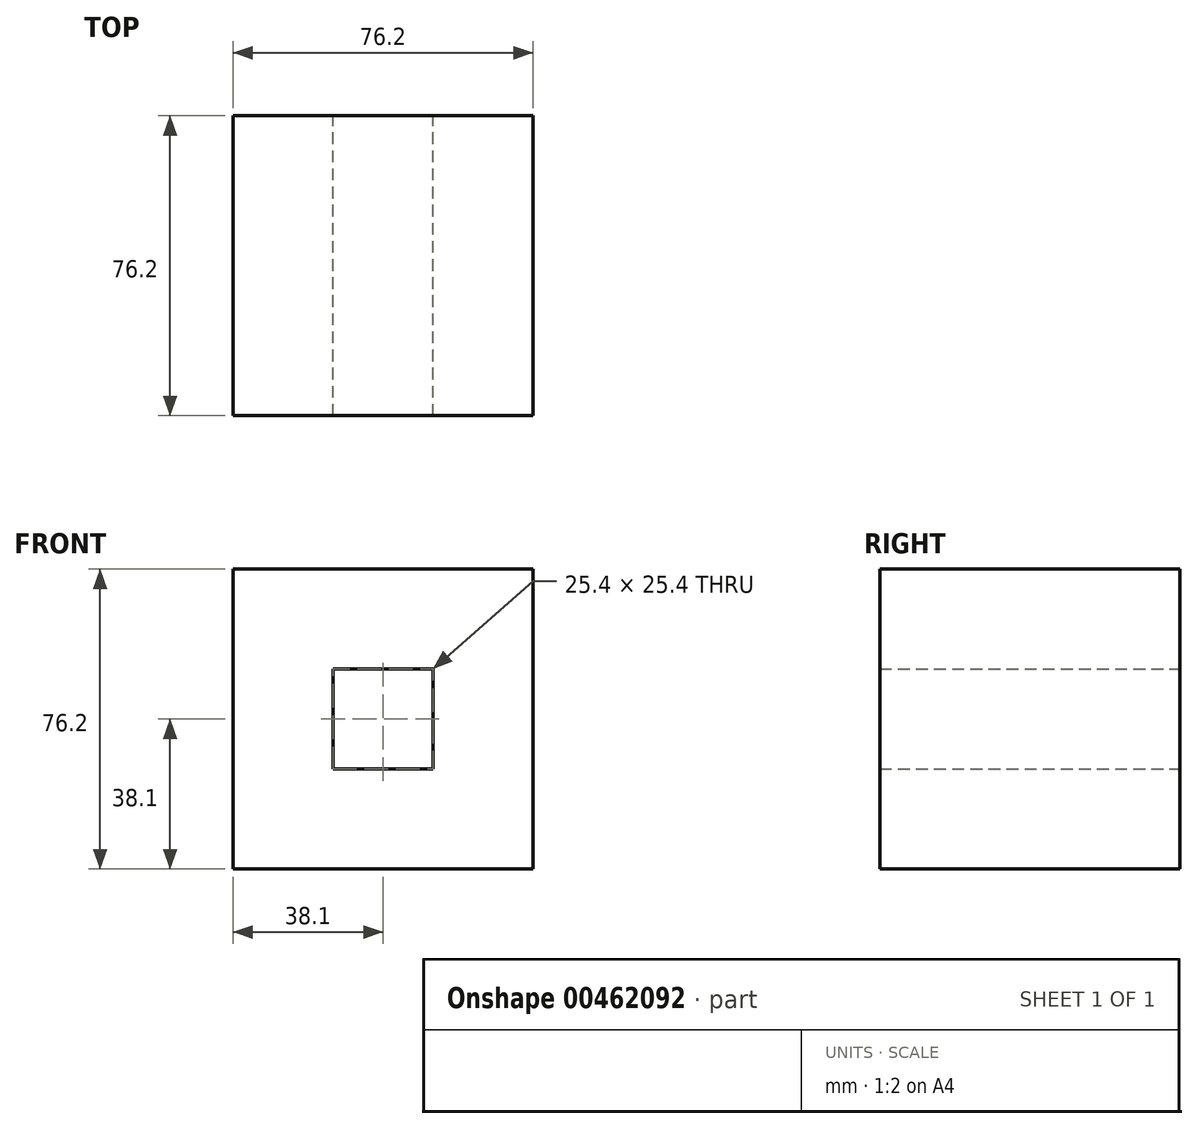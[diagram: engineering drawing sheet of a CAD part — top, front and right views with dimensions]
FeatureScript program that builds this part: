
annotation { "Feature Type Name" : "Feature", "Feature Type Description" : "" }
export const myFeature = defineFeature(function(context is Context, id is Id, definition is map)
    precondition{}
    {
        {
            var Q0;
            Q0=qCreatedBy(makeId("Front.planeOp"),FACE);
            var sketch = newSketch(context, id + "F0", { "sketchPlane" : qUnion([Q0])});
            skLineSegment(sketch, "E0.bottom", {"start": v(-38.1, 38.1) * mm, "end": v(38.1, 38.1) * mm});
            skLineSegment(sketch, "E0.top", {"start": v(-38.1, -38.1) * mm, "end": v(38.1, -38.1) * mm});
            skLineSegment(sketch, "E0.left", {"start": v(-38.1, 38.1) * mm, "end": v(-38.1, -38.1) * mm});
            skLineSegment(sketch, "E0.right", {"start": v(38.1, 38.1) * mm, "end": v(38.1, -38.1) * mm});
            skPoint(sketch, "E0.middle", {"position": v(0, 0) * mm});
            skLineSegment(sketch, "E1.bottom", {"start": v(12.7, 12.7) * mm, "end": v(-12.7, 12.7) * mm});
            skLineSegment(sketch, "E1.top", {"start": v(12.7, -12.7) * mm, "end": v(-12.7, -12.7) * mm});
            skLineSegment(sketch, "E1.left", {"start": v(12.7, 12.7) * mm, "end": v(12.7, -12.7) * mm});
            skLineSegment(sketch, "E1.right", {"start": v(-12.7, 12.7) * mm, "end": v(-12.7, -12.7) * mm});
            skSolve(sketch);
        }
        {
            var Q0;
            Q0=makeQuery(id+"F0.imprint","IMPRINT",FACE,{"disambiguationData":[TD([[makeQuery(id+"F0.imprint","IMPRINT",EDGE,{"derivedFrom":sQuery(id+"F0.wireOp",EDGE,"E0.bottom")}),-1.0]])]});
            extrude(context, id + "F1", {"entities" : qUnion([Q0]), "depth" : 76.2 * mm});
        }
    });
